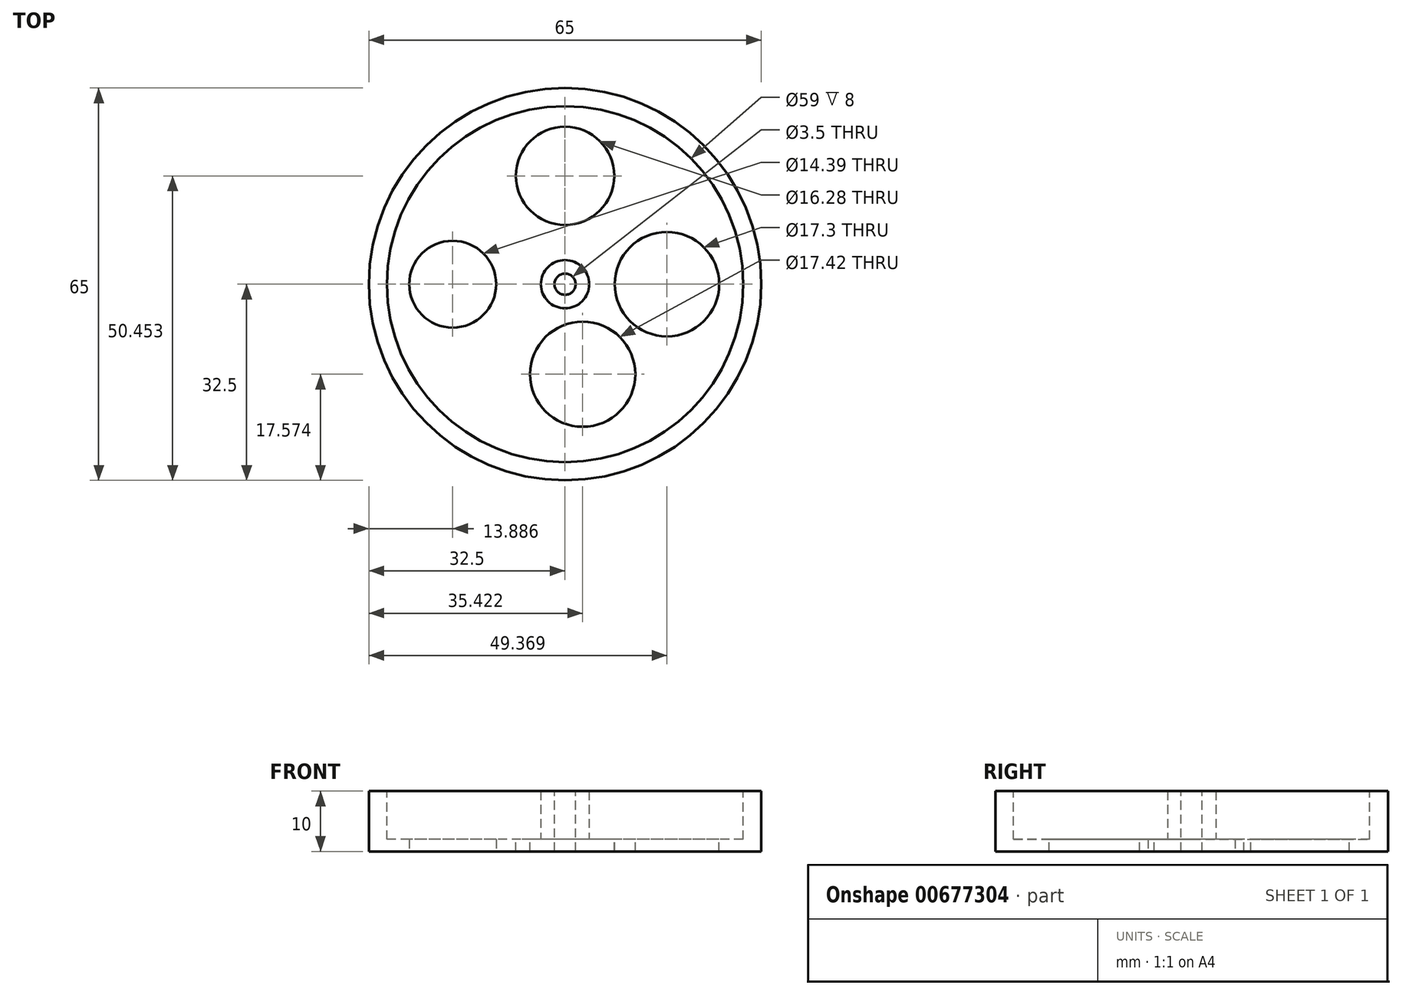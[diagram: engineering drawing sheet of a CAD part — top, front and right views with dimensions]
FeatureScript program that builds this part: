
annotation { "Feature Type Name" : "Feature", "Feature Type Description" : "" }
export const myFeature = defineFeature(function(context is Context, id is Id, definition is map)
    precondition{}
    {
        {
            var Q0;
            Q0=qCreatedBy(makeId("Top.planeOp"),FACE);
            var sketch = newSketch(context, id + "F0", { "sketchPlane" : qUnion([Q0])});
            skCircle(sketch, "E0", {"center": v(0, 0) * mm, "radius": 32.5 * mm});
            skSolve(sketch);
        }
        {
            var Q0;
            Q0=makeQuery(id+"F0.imprint","IMPRINT",FACE,{"disambiguationData":[TD([[makeQuery(id+"F0.imprint","IMPRINT",EDGE,{"derivedFrom":sQuery(id+"F0.wireOp",EDGE,"E0")}),1.0]])]});
            extrude(context, id + "F1", {"entities" : qUnion([Q0]), "depth" : 10 * mm, "offsetDistance" : 25 * mm});
        }
        {
            var Q0;
            Q0=makeQuery(id+"F1.opExtrude","CAP_FACE",FACE,{"disambiguationData":[OSD([sQuery(id+"F0.wireOp",EDGE,"E0")])],"isStart":false});
            var sketch = newSketch(context, id + "F2", { "sketchPlane" : qUnion([Q0])});
            skCircle(sketch, "E1", {"center": v(0, 0) * mm, "radius": 29.5 * mm});
            skSolve(sketch);
        }
        {
            var Q0;
            Q0=makeQuery(id+"F2.imprint","IMPRINT",FACE,{"disambiguationData":[TD([[makeQuery(id+"F2.imprint","IMPRINT",EDGE,{"derivedFrom":sQuery(id+"F2.wireOp",EDGE,"E1")}),1.0]])]});
            extrude(context, id + "F3", {"entities" : qUnion([Q0]), "operationType" : NewBodyOperationType.REMOVE, "oppositeDirection" : true, "depth" : 8 * mm, "offsetDistance" : 25 * mm});
        }
        {
            var Q0;
            Q0=makeQuery(id+"F3.boolean.opBoolean","COPY",FACE,{"derivedFrom":makeQuery(id+"F3.opExtrude","CAP_FACE",FACE,{"disambiguationData":[OSD([sQuery(id+"F2.wireOp",EDGE,"E1")])],"isStart":false})});
            var sketch = newSketch(context, id + "F4", { "sketchPlane" : qUnion([Q0])});
            skCircle(sketch, "E2", {"center": v(0, 0) * mm, "radius": 4 * mm});
            skSolve(sketch);
        }
        {
            var Q0;
            Q0=makeQuery(id+"F4.imprint","IMPRINT",FACE,{"disambiguationData":[TD([[makeQuery(id+"F4.imprint","IMPRINT",EDGE,{"derivedFrom":sQuery(id+"F4.wireOp",EDGE,"E2")}),1.0]])]});
            extrude(context, id + "F5", {"entities" : qUnion([Q0]), "operationType" : NewBodyOperationType.ADD, "depth" : 8 * mm, "offsetDistance" : 25 * mm});
        }
        {
            var Q0;
            Q0=makeQuery(id+"F5.opExtrude","CAP_FACE",FACE,{"disambiguationData":[OSD([sQuery(id+"F4.wireOp",EDGE,"E2")])],"isStart":false});
            var sketch = newSketch(context, id + "F6", { "sketchPlane" : qUnion([Q0])});
            skPoint(sketch, "E3", {"position": v(0, 0) * mm});
            skSolve(sketch);
        }
        {
            var Q0;
            Q0=sQuery(id+"F6.wireOp",VERTEX,"E3");
            var Q1;
            Q1=makeQuery(id+"F1.opExtrude","SWEPT_BODY",BODY,{"disambiguationData":[OSD([sQuery(id+"F0.wireOp",EDGE,"E0")])]});
            hole(context, id + "F7", {"style" : HoleStyle.SIMPLE, "endStyle" : HoleEndStyle.THROUGH, "holeDiameter" : 3.5 * mm, "majorDiameter" : 5 * mm, "isTappedThrough" : true, "tappedDepth" : 12 * mm, "tapClearance" : 3, "locations" : qUnion([Q0]), "scope" : qUnion([Q1])});
        }
        {
            var Q0;
            Q0=makeQuery(id+"F3.boolean.opBoolean","COPY",FACE,{"derivedFrom":makeQuery(id+"F3.opExtrude","CAP_FACE",FACE,{"disambiguationData":[OSD([sQuery(id+"F2.wireOp",EDGE,"E1")])],"isStart":false})});
            var sketch = newSketch(context, id + "F8", { "sketchPlane" : qUnion([Q0])});
            skSolve(sketch);
        }
        {
            var Q0;
            Q0=qCreatedBy(makeId("Top.planeOp"),FACE);
            var sketch = newSketch(context, id + "F9", { "sketchPlane" : qUnion([Q0])});
            skCircle(sketch, "E4", {"center": v(-17.95, -5.98) * mm, "radius": 7.59 * mm});
            skSolve(sketch);
        }
        {
            var Q0;
            Q0 = qSketchRegion(id + "F9", true);
            extrude(context, id + "F10", {"entities" : qUnion([Q0]), "operationType" : NewBodyOperationType.REMOVE, "oppositeDirection" : true, "depth" : 25 * mm, "offsetDistance" : 25 * mm});
        }
        {
            var Q0;
            Q0=qCreatedBy(makeId("Top.planeOp"),FACE);
            var sketch = newSketch(context, id + "F11", { "sketchPlane" : qUnion([Q0])});
            skCircle(sketch, "E5", {"center": v(-18.61, 0) * mm, "radius": 7.2 * mm});
            skSolve(sketch);
        }
        {
            var Q0;
            Q0 = qSketchRegion(id + "F11", true);
            extrude(context, id + "F12", {"entities" : qUnion([Q0]), "operationType" : NewBodyOperationType.REMOVE, "depth" : 8 * mm, "offsetDistance" : 25 * mm});
        }
        {
            var Q0;
            Q0=makeQuery(id+"F8.imprint","IMPRINT",FACE,{"disambiguationData":[TD([[makeQuery(id+"F8.imprint","IMPRINT",EDGE,{"derivedFrom":makeQuery(id+"F3.boolean.opBoolean","COPY",EDGE,{"derivedFrom":makeQuery(id+"F3.opExtrude","CAP_EDGE",EDGE,{"disambiguationData":[OSD([sQuery(id+"F2.wireOp",EDGE,"E1")])],"isStart":false})})}),1.0]])]});
            var sketch = newSketch(context, id + "F13", { "sketchPlane" : qUnion([Q0])});
            skCircle(sketch, "E6", {"center": v(0, 17.95) * mm, "radius": 8.14 * mm});
            skSolve(sketch);
        }
        {
            var Q0;
            Q0 = qSketchRegion(id + "F13", true);
            extrude(context, id + "F14", {"entities" : qUnion([Q0]), "operationType" : NewBodyOperationType.REMOVE, "oppositeDirection" : true, "depth" : 8 * mm, "offsetDistance" : 25 * mm});
        }
        {
            var Q0;
            Q0=qCreatedBy(makeId("Top.planeOp"),FACE);
            var sketch = newSketch(context, id + "F15", { "sketchPlane" : qUnion([Q0])});
            skCircle(sketch, "E7", {"center": v(-3.72, -14.25) * mm, "radius": 9.18 * mm});
            skSolve(sketch);
        }
        {
            var Q0;
            Q0 = qSketchRegion(id + "F15", true);
            extrude(context, id + "F16", {"entities" : qUnion([Q0]), "operationType" : NewBodyOperationType.REMOVE, "oppositeDirection" : true, "depth" : 8 * mm, "offsetDistance" : 25 * mm});
        }
        {
            var Q0;
            Q0=qCreatedBy(makeId("Top.planeOp"),FACE);
            var sketch = newSketch(context, id + "F17", { "sketchPlane" : qUnion([Q0])});
            skCircle(sketch, "E8", {"center": v(0, -15.32) * mm, "radius": 9.47 * mm});
            skSolve(sketch);
        }
        {
            var Q0;
            Q0 = qSketchRegion(id + "F17", true);
            extrude(context, id + "F18", {"entities" : qUnion([Q0]), "operationType" : NewBodyOperationType.REMOVE, "oppositeDirection" : true, "depth" : 8 * mm, "offsetDistance" : 25 * mm});
        }
        {
            var Q0;
            Q0=qCreatedBy(makeId("Top.planeOp"),FACE);
            var sketch = newSketch(context, id + "F19", { "sketchPlane" : qUnion([Q0])});
            skCircle(sketch, "E9", {"center": v(15.63, 0) * mm, "radius": 8.62 * mm});
            skSolve(sketch);
        }
        {
            var Q0;
            Q0 = qSketchRegion(id + "F19", true);
            extrude(context, id + "F20", {"entities" : qUnion([Q0]), "operationType" : NewBodyOperationType.REMOVE, "oppositeDirection" : true, "depth" : 8 * mm, "offsetDistance" : 25 * mm});
        }
        {
            var Q0;
            Q0=makeQuery(id+"F8.imprint","IMPRINT",FACE,{"disambiguationData":[TD([[makeQuery(id+"F8.imprint","IMPRINT",EDGE,{"derivedFrom":makeQuery(id+"F3.boolean.opBoolean","COPY",EDGE,{"derivedFrom":makeQuery(id+"F3.opExtrude","CAP_EDGE",EDGE,{"disambiguationData":[OSD([sQuery(id+"F2.wireOp",EDGE,"E1")])],"isStart":false})})}),1.0]])]});
            var sketch = newSketch(context, id + "F21", { "sketchPlane" : qUnion([Q0])});
            skCircle(sketch, "E10", {"center": v(16.87, 0) * mm, "radius": 8.65 * mm});
            skSolve(sketch);
        }
        {
            var Q0;
            Q0=makeQuery(id+"F21.imprint","IMPRINT",FACE,{"disambiguationData":[TD([[makeQuery(id+"F21.imprint","IMPRINT",EDGE,{"derivedFrom":sQuery(id+"F21.wireOp",EDGE,"E10")}),1.0]])]});
            extrude(context, id + "F22", {"entities" : qUnion([Q0]), "operationType" : NewBodyOperationType.REMOVE, "oppositeDirection" : true, "depth" : 8 * mm, "offsetDistance" : 25 * mm});
        }
        {
            var Q0;
            Q0=makeQuery(id+"F8.imprint","IMPRINT",FACE,{"disambiguationData":[TD([[makeQuery(id+"F8.imprint","IMPRINT",EDGE,{"derivedFrom":makeQuery(id+"F3.boolean.opBoolean","COPY",EDGE,{"derivedFrom":makeQuery(id+"F3.opExtrude","CAP_EDGE",EDGE,{"disambiguationData":[OSD([sQuery(id+"F2.wireOp",EDGE,"E1")])],"isStart":false})})}),1.0]])]});
            var sketch = newSketch(context, id + "F23", { "sketchPlane" : qUnion([Q0])});
            skCircle(sketch, "E11", {"center": v(-4.68, -11.26) * mm, "radius": 7.54 * mm});
            skSolve(sketch);
        }
        {
            var Q0;
            Q0=makeQuery(id+"F23.imprint","IMPRINT",FACE,{"disambiguationData":[TD([[makeQuery(id+"F23.imprint","IMPRINT",EDGE,{"derivedFrom":sQuery(id+"F23.wireOp",EDGE,"E11")}),1.0]])]});
            extrude(context, id + "F24", {"entities" : qUnion([Q0]), "operationType" : NewBodyOperationType.ADD, "oppositeDirection" : true, "depth" : 2 * mm, "offsetDistance" : 25 * mm});
        }
        {
            var Q0;
            Q0=makeQuery(id+"F8.imprint","IMPRINT",FACE,{"disambiguationData":[TD([[makeQuery(id+"F8.imprint","IMPRINT",EDGE,{"derivedFrom":makeQuery(id+"F3.boolean.opBoolean","COPY",EDGE,{"derivedFrom":makeQuery(id+"F3.opExtrude","CAP_EDGE",EDGE,{"disambiguationData":[OSD([sQuery(id+"F2.wireOp",EDGE,"E1")])],"isStart":false})})}),1.0]])]});
            var sketch = newSketch(context, id + "F25", { "sketchPlane" : qUnion([Q0])});
            skCircle(sketch, "E12", {"center": v(0, -16.62) * mm, "radius": 9.25 * mm});
            skSolve(sketch);
        }
        {
            var Q0;
            Q0=makeQuery(id+"F25.imprint","IMPRINT",FACE,{"disambiguationData":[TD([[makeQuery(id+"F25.imprint","IMPRINT",EDGE,{"derivedFrom":sQuery(id+"F25.wireOp",EDGE,"E12")}),1.0]])]});
            extrude(context, id + "F26", {"entities" : qUnion([Q0]), "operationType" : NewBodyOperationType.ADD, "oppositeDirection" : true, "depth" : 2 * mm, "offsetDistance" : 25 * mm});
        }
        {
            var Q0;
            Q0=makeQuery(id+"F8.imprint","IMPRINT",FACE,{"disambiguationData":[TD([[makeQuery(id+"F8.imprint","IMPRINT",EDGE,{"derivedFrom":makeQuery(id+"F3.boolean.opBoolean","COPY",EDGE,{"derivedFrom":makeQuery(id+"F3.opExtrude","CAP_EDGE",EDGE,{"disambiguationData":[OSD([sQuery(id+"F2.wireOp",EDGE,"E1")])],"isStart":false})})}),1.0]])]});
            var sketch = newSketch(context, id + "F27", { "sketchPlane" : qUnion([Q0])});
            skCircle(sketch, "E13", {"center": v(-4.2, -15.14) * mm, "radius": 9.86 * mm});
            skSolve(sketch);
        }
        {
            var Q0;
            Q0=makeQuery(id+"F27.imprint","IMPRINT",FACE,{"disambiguationData":[TD([[makeQuery(id+"F27.imprint","IMPRINT",EDGE,{"derivedFrom":sQuery(id+"F27.wireOp",EDGE,"E13")}),1.0]])]});
            extrude(context, id + "F28", {"entities" : qUnion([Q0]), "operationType" : NewBodyOperationType.ADD, "oppositeDirection" : true, "depth" : 2 * mm, "offsetDistance" : 25 * mm});
        }
        {
            var Q0;
            Q0=makeQuery(id+"F8.imprint","IMPRINT",FACE,{"disambiguationData":[TD([[makeQuery(id+"F8.imprint","IMPRINT",EDGE,{"derivedFrom":makeQuery(id+"F3.boolean.opBoolean","COPY",EDGE,{"derivedFrom":makeQuery(id+"F3.opExtrude","CAP_EDGE",EDGE,{"disambiguationData":[OSD([sQuery(id+"F2.wireOp",EDGE,"E1")])],"isStart":false})})}),1.0]])]});
            var sketch = newSketch(context, id + "F29", { "sketchPlane" : qUnion([Q0])});
            skCircle(sketch, "E14", {"center": v(2.92, -14.93) * mm, "radius": 8.7 * mm});
            skSolve(sketch);
        }
        {
            var Q0;
            Q0=makeQuery(id+"F29.imprint","IMPRINT",FACE,{"disambiguationData":[TD([[makeQuery(id+"F29.imprint","IMPRINT",EDGE,{"derivedFrom":sQuery(id+"F29.wireOp",EDGE,"E14")}),1.0]])]});
            extrude(context, id + "F30", {"entities" : qUnion([Q0]), "operationType" : NewBodyOperationType.REMOVE, "oppositeDirection" : true, "depth" : 25 * mm, "offsetDistance" : 25 * mm});
        }
    });
